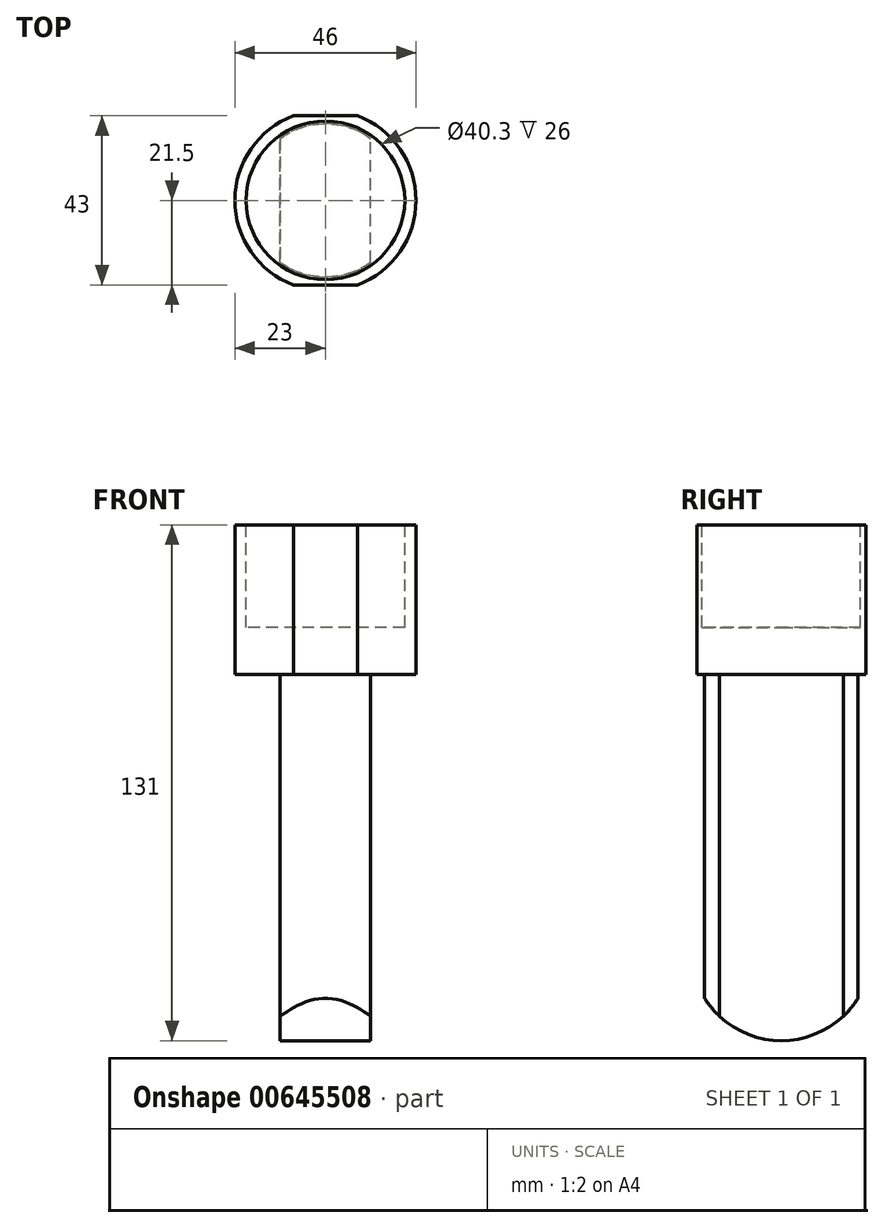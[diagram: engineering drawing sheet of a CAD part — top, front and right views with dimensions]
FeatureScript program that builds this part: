
annotation { "Feature Type Name" : "Feature", "Feature Type Description" : "" }
export const myFeature = defineFeature(function(context is Context, id is Id, definition is map)
    precondition{}
    {
        {
            var Q0;
            Q0=qCreatedBy(makeId("Top.planeOp"),FACE);
            var sketch = newSketch(context, id + "F0", { "sketchPlane" : qUnion([Q0])});
            skArc(sketch, "E0", {"start": v(-8.17, 21.5) * mm, "mid": v(-23, 0) * mm, "end": v(-8.17, -21.5) * mm});
            skLineSegment(sketch, "E1", {"start": v(-8.17, 21.5) * mm, "end": v(8.17, 21.5) * mm});
            skLineSegment(sketch, "E2.MirrorCS", {"start": v(-8.17, -21.5) * mm, "end": v(8.17, -21.5) * mm});
            skArc(sketch, "E3.trimOffspring", {"start": v(8.17, -21.5) * mm, "mid": v(23, 0) * mm, "end": v(8.17, 21.5) * mm});
            skSolve(sketch);
        }
        {
            var Q0;
            Q0 = qSketchRegion(id + "F0", true);
            extrude(context, id + "F1", {"entities" : qUnion([Q0]), "depth" : 38 * mm, "offsetDistance" : 25 * mm});
        }
        {
            var Q0;
            Q0=makeQuery(id+"F1.opExtrude","CAP_FACE",FACE,{"disambiguationData":[OSD([sQuery(id+"F0.wireOp",EDGE,"E0"),sQuery(id+"F0.wireOp",EDGE,"E1"),sQuery(id+"F0.wireOp",EDGE,"E2.MirrorCS"),sQuery(id+"F0.wireOp",EDGE,"E3.trimOffspring")])],"isStart":false});
            var sketch = newSketch(context, id + "F2", { "sketchPlane" : qUnion([Q0])});
            skCircle(sketch, "E4", {"center": v(0, 0) * mm, "radius": 20.15 * mm});
            skSolve(sketch);
        }
        {
            var Q0;
            Q0=makeQuery(id+"F2.imprint","IMPRINT",FACE,{"disambiguationData":[TD([[makeQuery(id+"F2.imprint","IMPRINT",EDGE,{"derivedFrom":sQuery(id+"F2.wireOp",EDGE,"E4")}),1.0]])]});
            extrude(context, id + "F3", {"entities" : qUnion([Q0]), "operationType" : NewBodyOperationType.REMOVE, "oppositeDirection" : true, "depth" : 26 * mm, "offsetDistance" : 25 * mm});
        }
        {
            var Q0;
            Q0=makeQuery(id+"F1.opExtrude","CAP_FACE",FACE,{"disambiguationData":[OSD([sQuery(id+"F0.wireOp",EDGE,"E0"),sQuery(id+"F0.wireOp",EDGE,"E1"),sQuery(id+"F0.wireOp",EDGE,"E2.MirrorCS"),sQuery(id+"F0.wireOp",EDGE,"E3.trimOffspring")])],"isStart":true});
            var sketch = newSketch(context, id + "F4", { "sketchPlane" : qUnion([Q0])});
            skArc(sketch, "E5", {"start": v(-11.5, -15.75) * mm, "mid": v(0, -19.5) * mm, "end": v(11.5, -15.75) * mm});
            skLineSegment(sketch, "E6", {"start": v(-11.5, 15.75) * mm, "end": v(-11.5, -15.75) * mm});
            skLineSegment(sketch, "E7.MirrorCS", {"start": v(11.5, 15.75) * mm, "end": v(11.5, -15.75) * mm});
            skArc(sketch, "E8.trimOffspring", {"start": v(11.5, 15.75) * mm, "mid": v(0, 19.5) * mm, "end": v(-11.5, 15.75) * mm});
            skSolve(sketch);
        }
        {
            var Q0;
            Q0=makeQuery(id+"F4.imprint","IMPRINT",FACE,{"disambiguationData":[TD([[makeQuery(id+"F4.imprint","IMPRINT",EDGE,{"derivedFrom":sQuery(id+"F4.wireOp",EDGE,"E5")}),1.0]])]});
            extrude(context, id + "F5", {"entities" : qUnion([Q0]), "operationType" : NewBodyOperationType.ADD, "depth" : 93 * mm, "offsetDistance" : 25 * mm});
        }
        {
            var Q0;
            Q0=makeQuery(id+"F5.opExtrude","SWEPT_FACE",FACE,{"disambiguationData":[OSD([sQuery(id+"F4.wireOp",EDGE,"E6")])]});
            var sketch = newSketch(context, id + "F6", { "sketchPlane" : qUnion([Q0])});
            skArc(sketch, "E9", {"start": v(-22.12, -76.3) * mm, "mid": v(0.4, -93) * mm, "end": v(22.33, -75.53) * mm});
            skLineSegment(sketch, "E10", {"start": v(-22.12, -76.3) * mm, "end": v(-36.34, -104.3) * mm});
            skLineSegment(sketch, "E11", {"start": v(-36.34, -104.3) * mm, "end": v(35.98, -104.3) * mm});
            skLineSegment(sketch, "E12", {"start": v(35.98, -104.3) * mm, "end": v(22.33, -75.53) * mm});
            skSolve(sketch);
        }
        {
            var Q0;
            {var subQ0=sQuery(id+"F6.wireOp",EDGE,"E9");var subQ1=sQuery(id+"F4.wireOp",EDGE,"E6");var subQ4=makeQuery(id+"F5.opExtrude","CAP_EDGE",EDGE,{"disambiguationData":[OSD([subQ1])],"isStart":false});var subQ5=makeQuery(id+"F6.imprint","INTERSECT",VERTEX,{"derivedFrom":[subQ4,subQ0]});Q0=makeQuery(id+"F6.imprint","IMPRINT",FACE,{"disambiguationData":[TD([[makeQuery(id+"F6.imprint","IMPRINT",EDGE,{"disambiguationData":[TD([[subQ5,1.0]])],"derivedFrom":subQ0}),-1.0]])]});}
            var Q1;
            {var subQ0=sQuery(id+"F6.wireOp",EDGE,"E9");var subQ1=sQuery(id+"F4.wireOp",EDGE,"E6");var subQ4=makeQuery(id+"F5.opExtrude","CAP_EDGE",EDGE,{"disambiguationData":[OSD([subQ1])],"isStart":false});var subQ5=makeQuery(id+"F6.imprint","INTERSECT",VERTEX,{"derivedFrom":[subQ4,subQ0]});Q1=makeQuery(id+"F6.imprint","IMPRINT",FACE,{"disambiguationData":[TD([[makeQuery(id+"F6.imprint","IMPRINT",EDGE,{"disambiguationData":[TD([[subQ5,-1.0]])],"derivedFrom":subQ0}),-1.0]])]});}
            var Q2;
            {var subQ0=sQuery(id+"F6.wireOp",EDGE,"E10");Q2=makeQuery(id+"F6.imprint","IMPRINT",FACE,{"disambiguationData":[TD([[makeQuery(id+"F6.imprint","IMPRINT",EDGE,{"derivedFrom":subQ0}),1.0]])]});}
            extrude(context, id + "F7", {"entities" : qUnion([Q0, Q1, Q2]), "operationType" : NewBodyOperationType.REMOVE, "endBound" : BoundingType.THROUGH_ALL, "oppositeDirection" : true, "depth" : 25 * mm, "offsetDistance" : 25 * mm});
        }
    });
